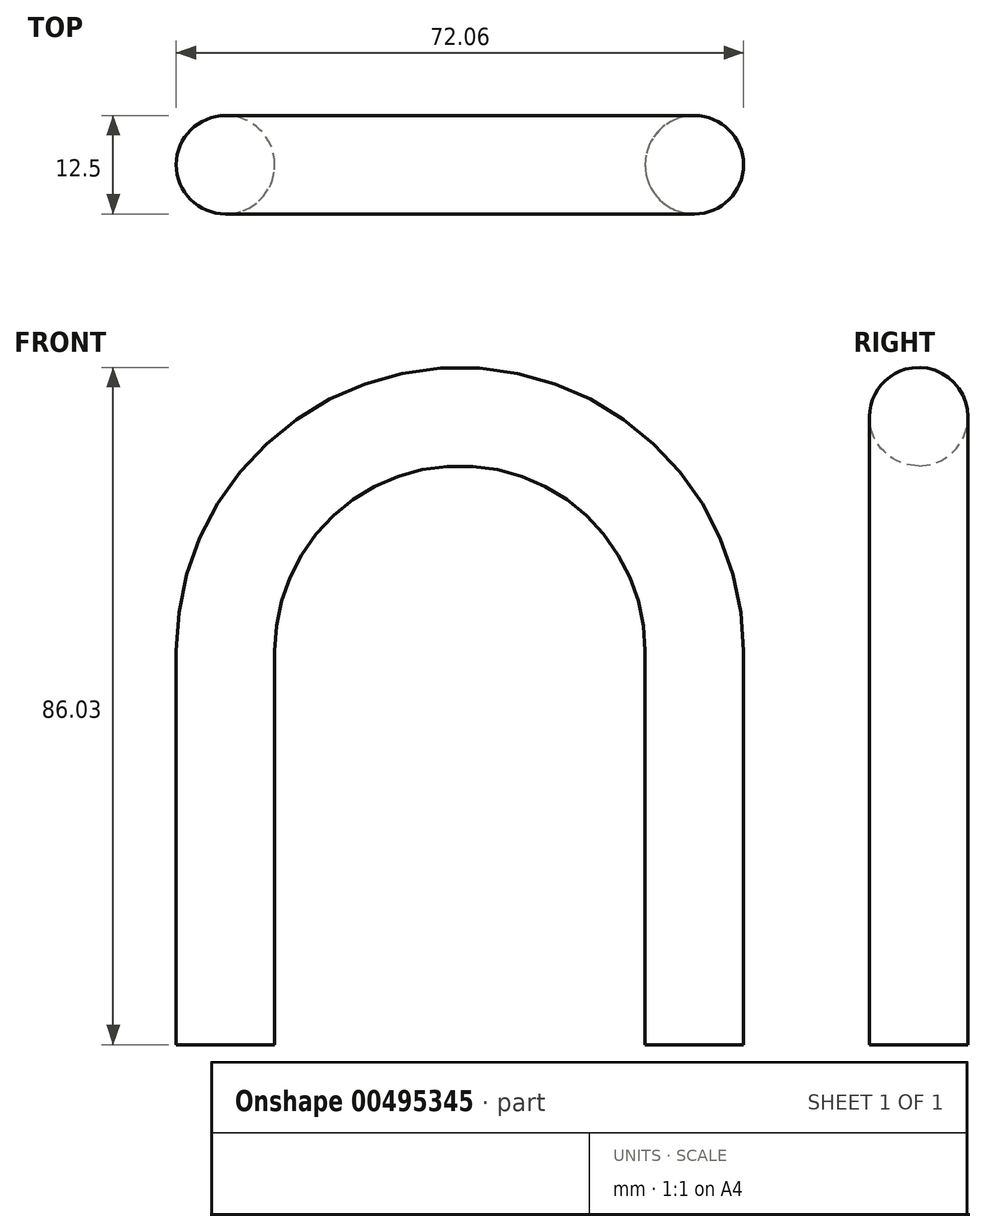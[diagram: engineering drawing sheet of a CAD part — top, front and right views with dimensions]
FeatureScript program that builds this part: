
annotation { "Feature Type Name" : "Feature", "Feature Type Description" : "" }
export const myFeature = defineFeature(function(context is Context, id is Id, definition is map)
    precondition{}
    {
        {
            var Q0;
            Q0=qCreatedBy(makeId("Front.planeOp"),FACE);
            var sketch = newSketch(context, id + "F0", { "sketchPlane" : qUnion([Q0])});
            skLineSegment(sketch, "E0", {"start": v(-30, 0) * mm, "end": v(-30, 50) * mm});
            skArc(sketch, "E1", {"start": v(-30, 50) * mm, "mid": v(-21.21, 71.21) * mm, "end": v(0, 80) * mm});
            skLineSegment(sketch, "E2", {"start": v(0, 91.4) * mm, "end": v(0, -17.16) * mm, "construction": true});
            skArc(sketch, "E3.MirrorCS", {"start": v(30, 50) * mm, "mid": v(21.21, 71.21) * mm, "end": v(0, 80) * mm});
            skLineSegment(sketch, "E4.MirrorCS", {"start": v(30, 0) * mm, "end": v(30, 50) * mm});
            skSolve(sketch);
        }
        {
            var Q0;
            Q0=qCreatedBy(makeId("Top.planeOp"),FACE);
            var sketch = newSketch(context, id + "F1", { "sketchPlane" : qUnion([Q0])});
            skCircle(sketch, "E5", {"center": v(-29.78, 0) * mm, "radius": 6.25 * mm});
            skSolve(sketch);
        }
        {
            var Q0;
            Q0=makeQuery(id+"F1.imprint","IMPRINT",FACE,{"disambiguationData":[TD([[makeQuery(id+"F1.imprint","IMPRINT",EDGE,{"derivedFrom":sQuery(id+"F1.wireOp",EDGE,"E5")}),1.0]])]});
            var Q1;
            Q1=sQuery(id+"F0.wireOp",EDGE,"E1");
            var Q2;
            Q2=sQuery(id+"F0.wireOp",EDGE,"E0");
            var Q3;
            Q3=sQuery(id+"F0.wireOp",EDGE,"E3.MirrorCS");
            var Q4;
            Q4=sQuery(id+"F0.wireOp",EDGE,"E4.MirrorCS");
            sweep(context, id + "F2", {"profiles" : qUnion([Q0]), "path" : qUnion([Q1, Q2, Q3, Q4])});
        }
    });
